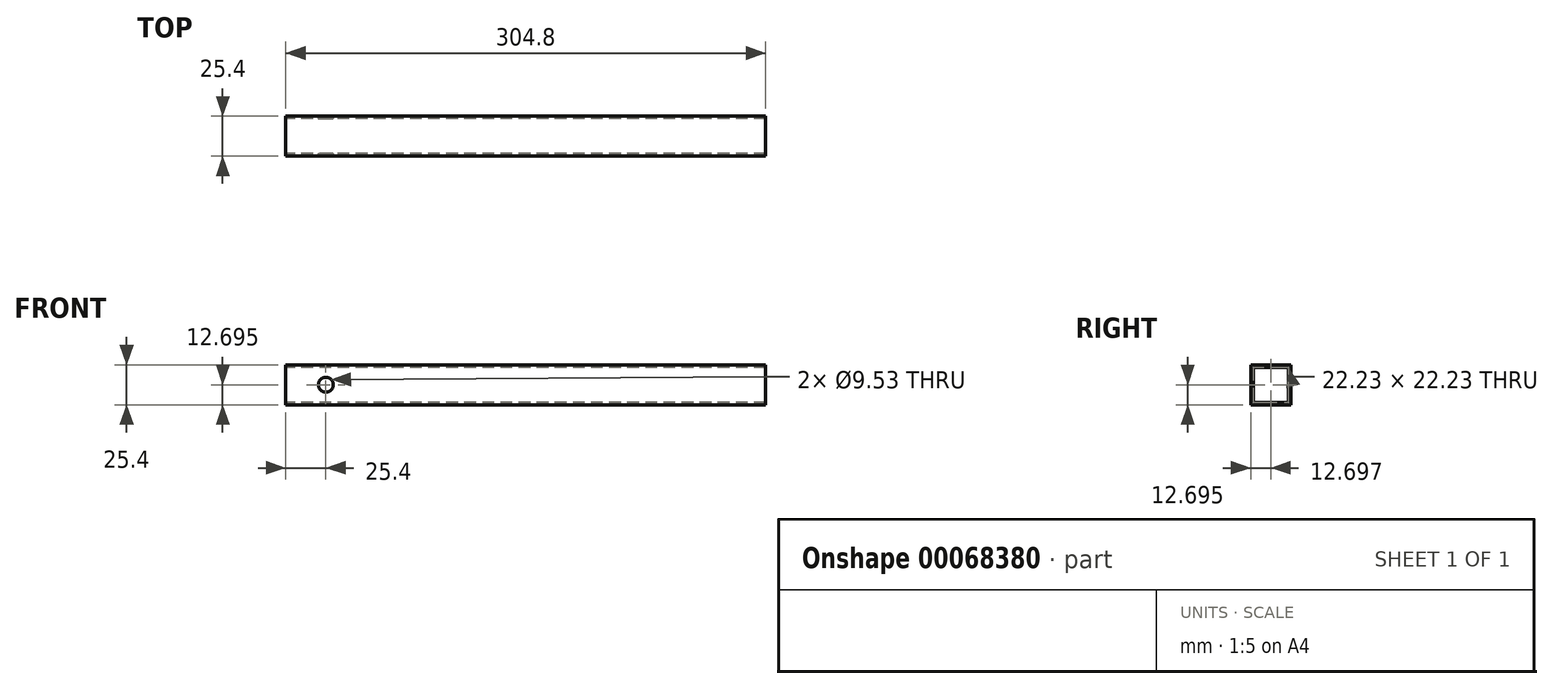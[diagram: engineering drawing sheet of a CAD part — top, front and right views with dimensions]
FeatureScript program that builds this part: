
annotation { "Feature Type Name" : "Feature", "Feature Type Description" : "" }
export const myFeature = defineFeature(function(context is Context, id is Id, definition is map)
    precondition{}
    {
        {
            var Q0;
            Q0=qCreatedBy(makeId("Right.planeOp"),FACE);
            var sketch = newSketch(context, id + "F0", { "sketchPlane" : qUnion([Q0])});
            skLineSegment(sketch, "E0.bottom", {"start": v(1.59, -21.75) * mm, "end": v(-23.81, -21.75) * mm});
            skLineSegment(sketch, "E0.top", {"start": v(1.59, 3.65) * mm, "end": v(-23.81, 3.65) * mm});
            skLineSegment(sketch, "E0.left", {"start": v(1.59, -21.75) * mm, "end": v(1.59, 3.65) * mm});
            skLineSegment(sketch, "E0.right", {"start": v(-23.81, -21.75) * mm, "end": v(-23.81, 3.65) * mm});
            skLineSegment(sketch, "E1.bottom", {"start": v(0, -20.17) * mm, "end": v(-22.22, -20.17) * mm});
            skLineSegment(sketch, "E1.top", {"start": v(0, 2.06) * mm, "end": v(-22.23, 2.06) * mm});
            skLineSegment(sketch, "E1.left", {"start": v(0, -20.17) * mm, "end": v(0, 2.06) * mm});
            skLineSegment(sketch, "E1.right", {"start": v(-22.22, -20.17) * mm, "end": v(-22.23, 2.06) * mm});
            skSolve(sketch);
        }
        {
            var Q0;
            Q0 = qSketchRegion(id + "F0", true);
            extrude(context, id + "F1", {"entities" : qUnion([Q0]), "depth" : 304.8 * mm});
        }
        {
            var Q0;
            Q0=makeQuery(id+"F1.opExtrude","SWEPT_FACE",FACE,{"disambiguationData":[OSD([sQuery(id+"F0.wireOp",EDGE,"E0.right")])]});
            var sketch = newSketch(context, id + "F2", { "sketchPlane" : qUnion([Q0])});
            skCircle(sketch, "E2", {"center": v(25.4, -9.05) * mm, "radius": 4.76 * mm});
            skSolve(sketch);
        }
        {
            var Q0;
            Q0 = qSketchRegion(id + "F2", true);
            extrude(context, id + "F3", {"entities" : qUnion([Q0]), "operationType" : NewBodyOperationType.REMOVE, "oppositeDirection" : true, "depth" : 25.4 * mm});
        }
    });
